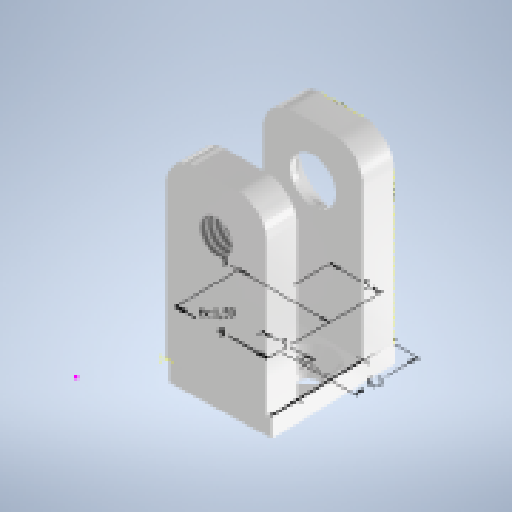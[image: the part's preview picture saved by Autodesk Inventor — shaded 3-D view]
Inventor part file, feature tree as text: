
AUTODESK INVENTOR PART (.ipt)
format: ipt  version: 2025 (Build 290162010, 162A)  size: 232,960 bytes
history: native  units: mm
features: sketch x3, hole x3, extrude x2, fillet x1
ambient origin geometry x8: Origin, YZ Plane, XZ Plane, XY Plane, X Axis, Y Axis, Z Axis, Center Point
bodies: Volumenkörper1 (feature_tree)
feature tree (9):
  extrude  "Extrusion1"  Depth=3.0mm
  fillet  "Rundung1"  Radius=3.0mm
  sketch  "Skizze2"  dims[d3=6.6mm d5=18.0mm d6=0.0mm]
  hole  "Bohrung1"  [1 undecoded]
  sketch  "Skizze4"  dims[d7=3.0mm d8=4.3mm d9=8.0mm d10=9.4mm d11=14.0mm d12=90.0deg d13=11.8mm d14=20.594885mm d19=2.0mm d20=8.0mm d21=5.0mm d22=2.0mm d23=90.0deg d24=8.0mm d25=20.594885mm d34=5.0mm d35=9.0mm d36=6.3mm d37=5.0mm d38=9.0mm d40=9.0mm d41=-0.277101mm d42=2.0mm d43=0.0mm d44=3.242mm d45=8.0mm d46=9.0mm d47=2.0mm d48=90.0deg d49=8.0mm d50=20.594885mm]
  extrude  "Extrusion3"  Depth=2.0mm
  hole  "Bohrung2"  [1 undecoded]
  hole  "Bohrung4"  [1 undecoded]
  sketch  "Skizze1"  dims[d0=10.0mm d1=3.0mm d2=3.0mm]
note: 3 required parameter values undecoded (feature->parameter linkage not recoverable at this tier; creation-order binding heuristic only, values carry confidence <= 0.55)
